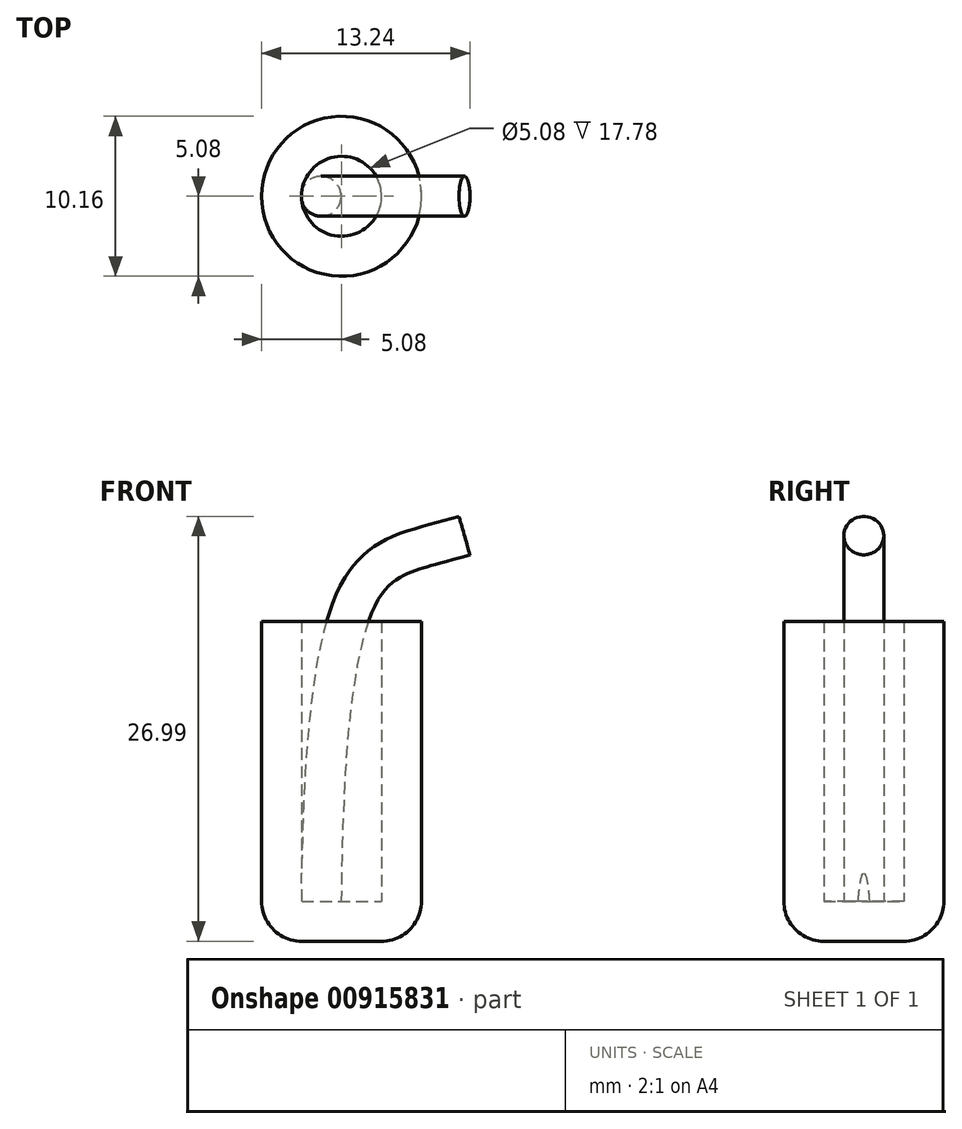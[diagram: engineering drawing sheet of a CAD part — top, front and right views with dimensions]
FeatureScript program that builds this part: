
annotation { "Feature Type Name" : "Feature", "Feature Type Description" : "" }
export const myFeature = defineFeature(function(context is Context, id is Id, definition is map)
    precondition{}
    {
        {
            var Q0;
            Q0=qCreatedBy(makeId("Front.planeOp"),FACE);
            var sketch = newSketch(context, id + "F0", { "sketchPlane" : qUnion([Q0])});
            skLineSegment(sketch, "E0.bottom", {"start": v(0, 0) * mm, "end": v(5.08, 0) * mm});
            skLineSegment(sketch, "E0.top", {"start": v(0, 20.32) * mm, "end": v(5.08, 20.32) * mm, "construction": true});
            skLineSegment(sketch, "E0.left", {"start": v(0, 0) * mm, "end": v(0, 20.32) * mm, "construction": true});
            skLineSegment(sketch, "E0.right", {"start": v(5.08, 0) * mm, "end": v(5.08, 20.32) * mm});
            skLineSegment(sketch, "E1", {"start": v(5.08, 20.32) * mm, "end": v(2.54, 20.32) * mm});
            skLineSegment(sketch, "E2", {"start": v(2.54, 2.54) * mm, "end": v(2.54, 20.32) * mm});
            skLineSegment(sketch, "E3", {"start": v(2.54, 2.54) * mm, "end": v(0, 2.54) * mm});
            skLineSegment(sketch, "E4", {"start": v(0, 2.54) * mm, "end": v(0, 0) * mm});
            skSolve(sketch);
        }
        {
            var Q0;
            Q0=qCreatedBy(makeId("Front.planeOp"),FACE);
            var sketch = newSketch(context, id + "F1", { "sketchPlane" : qUnion([Q0])});
            skFitSpline(sketch, "E5", {"points": [v(-1.3, 1.95) * mm, v(1.33, 22.5) * mm, v(4.37, 24.78) * mm, v(7.8, 25.76) * mm], "startDerivative": vector(0.45, 48.08) * mm, "endDerivative": vector(26.17, 7.48) * mm});
            skSolve(sketch);
        }
        {
            var Q0;
            Q0=makeQuery(id+"F0.imprint","IMPRINT",FACE,{"disambiguationData":[TD([[makeQuery(id+"F0.imprint","IMPRINT",EDGE,{"derivedFrom":sQuery(id+"F0.wireOp",EDGE,"E0.bottom")}),1.0]])]});
            var Q1;
            Q1=sQuery(id+"F0.wireOp",EDGE,"E0.left");
            revolve(context, id + "F2", {"surfaceOperationType" : NewSurfaceOperationType.NEW, "entities" : qUnion([Q0]), "axis" : qUnion([Q1]), "revolveType" : RevolveType.FULL});
        }
        {
            var Q0;
            Q0=sQuery(id+"F1.wireOp",VERTEX,"E5.end");
            var Q1;
            Q1=sQuery(id+"F1.wireOp",EDGE,"E5");
            cPlane(context, id + "F3", {"entities" : qUnion([Q0, Q1]), "cplaneType" : CPlaneType.CURVE_POINT, "offset" : 25.4 * mm, "width" : 152.4 * mm, "height" : 152.4 * mm});
        }
        {
            var Q0;
            Q0=qCreatedBy(id+"F3.planeOp",FACE);
            var sketch = newSketch(context, id + "F4", { "sketchPlane" : qUnion([Q0])});
            skCircle(sketch, "E6", {"center": v(0, 22.63) * mm, "radius": 1.27 * mm});
            skSolve(sketch);
        }
        {
            var Q0;
            Q0=makeQuery(id+"F4.imprint","IMPRINT",FACE,{"disambiguationData":[TD([[makeQuery(id+"F4.imprint","IMPRINT",EDGE,{"derivedFrom":sQuery(id+"F4.wireOp",EDGE,"E6")}),1.0]])]});
            var Q1;
            Q1=sQuery(id+"F4.wireOp",EDGE,"E6");
            var Q2;
            Q2=sQuery(id+"F1.wireOp",EDGE,"E5");
            sweep(context, id + "F5", {"operationType" : NewBodyOperationType.ADD, "profiles" : qUnion([Q0]), "surfaceOperationType" : NewSurfaceOperationType.ADD, "surfaceProfiles" : qUnion([Q1]), "path" : qUnion([Q2])});
        }
        {
            var Q0;
            Q0=makeQuery(id+"F2.opRevolve","SWEPT_EDGE",EDGE,{"disambiguationData":[OSD([sQuery(id+"F0.wireOp",EDGE,"E0.bottom"),sQuery(id+"F0.wireOp",EDGE,"E0.right")])]});
            fillet(context, id + "F6", {"entities" : qUnion([Q0]), "radius" : 2.54 * mm, "tangentPropagation" : true, "allowEdgeOverflow" : false});
        }
    });
